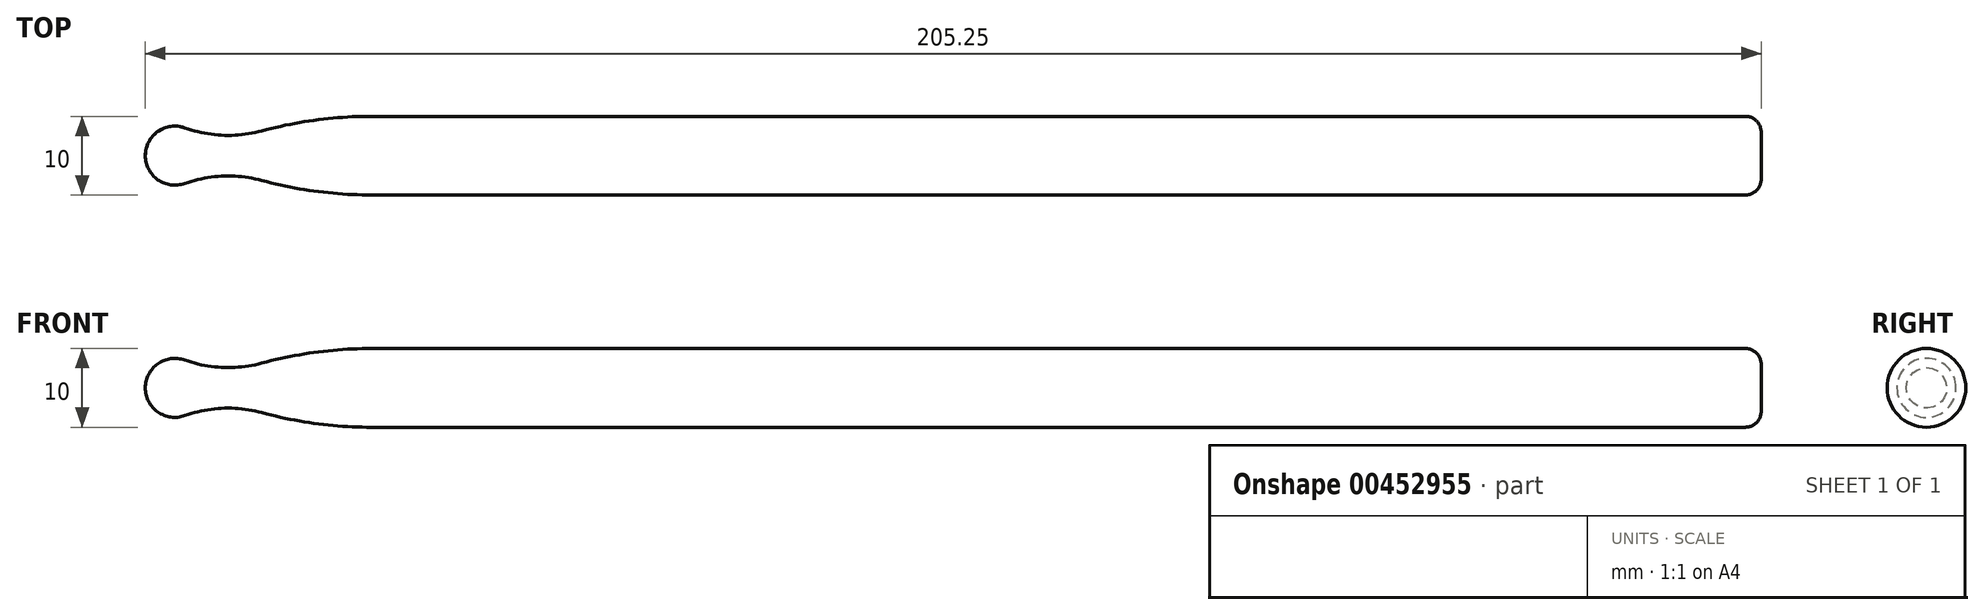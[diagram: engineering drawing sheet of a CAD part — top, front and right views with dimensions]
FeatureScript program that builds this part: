
annotation { "Feature Type Name" : "Feature", "Feature Type Description" : "" }
export const myFeature = defineFeature(function(context is Context, id is Id, definition is map)
    precondition{}
    {
        {
            var Q0;
            Q0=qCreatedBy(makeId("Top.planeOp"),FACE);
            var sketch = newSketch(context, id + "F0", { "sketchPlane" : qUnion([Q0])});
            skLineSegment(sketch, "E0", {"start": v(74.5, 5) * mm, "end": v(-100, 5) * mm});
            skArc(sketch, "E1", {"start": v(-123.74, 3.53) * mm, "mid": v(-118.88, 2.59) * mm, "end": v(-113.95, 3.14) * mm});
            skArc(sketch, "E2", {"start": v(-100, 5) * mm, "mid": v(-107.04, 4.53) * mm, "end": v(-113.95, 3.14) * mm});
            skArc(sketch, "E3", {"start": v(-123.74, 3.53) * mm, "mid": v(-127.16, 3.07) * mm, "end": v(-128.75, 0) * mm});
            skLineSegment(sketch, "E4", {"start": v(76.5, 3) * mm, "end": v(76.5, 0) * mm});
            skPoint(sketch, "E5.newPointB", {"position": v(75, 5) * mm});
            skArc(sketch, "E5.filletArc", {"start": v(76.5, 3) * mm, "mid": v(75.91, 4.41) * mm, "end": v(74.5, 5) * mm});
            skLineSegment(sketch, "E6", {"start": v(-128.75, 0) * mm, "end": v(76.5, 0) * mm});
            skSolve(sketch);
        }
        {
            var Q0;
            Q0=makeQuery(id+"F0.imprint","IMPRINT",FACE,{"disambiguationData":[TD([[makeQuery(id+"F0.imprint","IMPRINT",EDGE,{"derivedFrom":sQuery(id+"F0.wireOp",EDGE,"E0")}),1.0]])]});
            var Q1;
            Q1=sQuery(id+"F0.wireOp",EDGE,"E6");
            revolve(context, id + "F1", {"surfaceOperationType" : NewSurfaceOperationType.NEW, "entities" : qUnion([Q0]), "axis" : qUnion([Q1]), "revolveType" : RevolveType.FULL});
        }
    });
